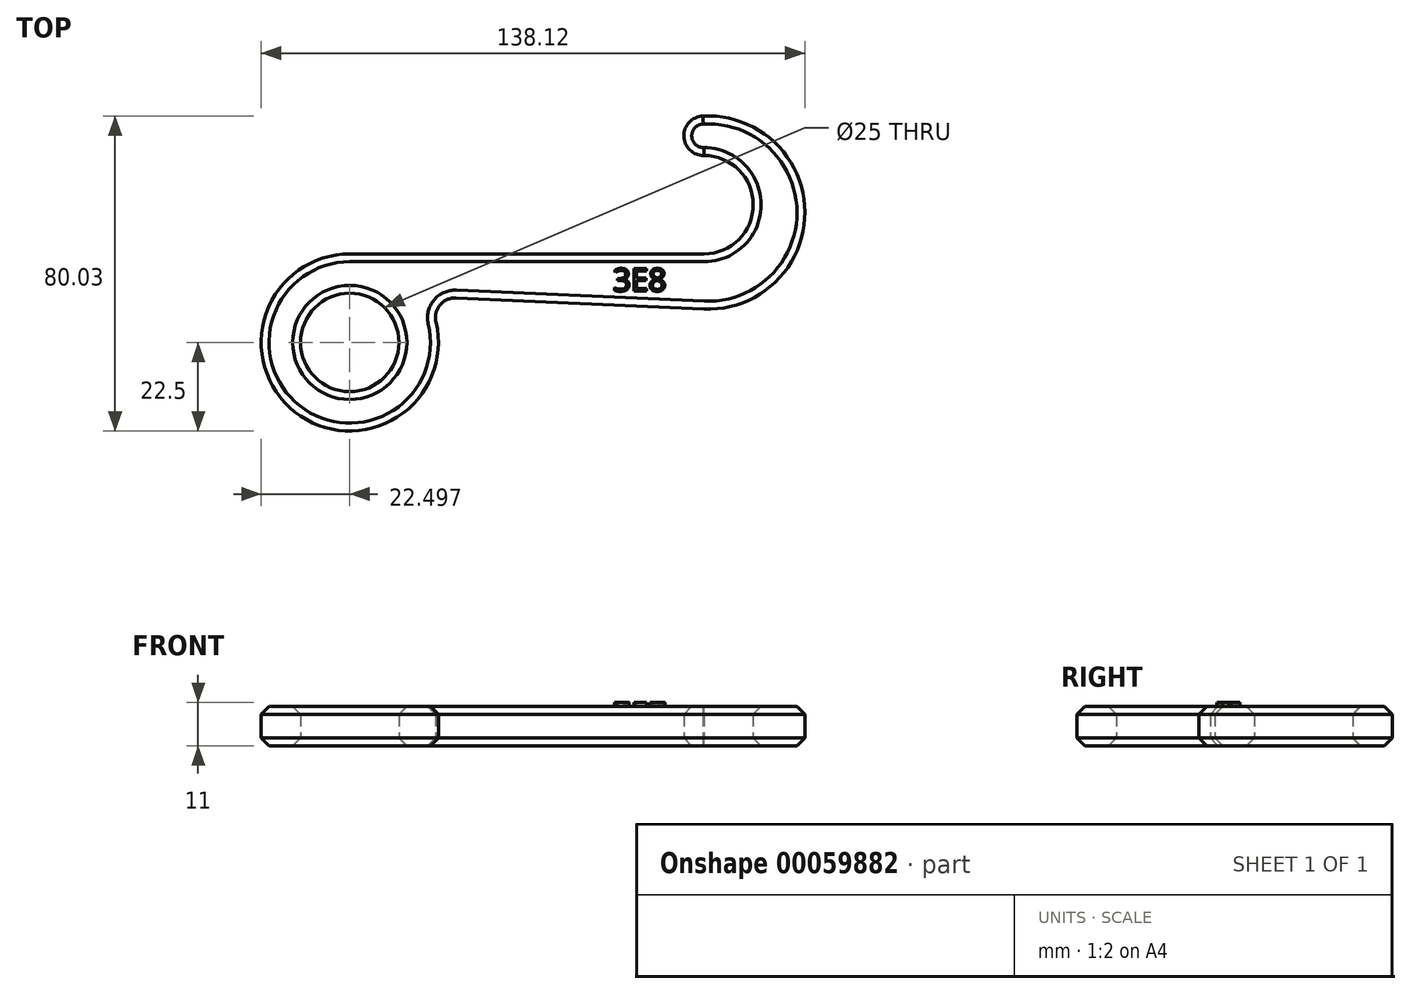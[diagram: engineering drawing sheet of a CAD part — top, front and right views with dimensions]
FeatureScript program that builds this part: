
annotation { "Feature Type Name" : "Feature", "Feature Type Description" : "" }
export const myFeature = defineFeature(function(context is Context, id is Id, definition is map)
    precondition{}
    {
        {
            var Q0;
            Q0=qCreatedBy(makeId("Top.planeOp"),FACE);
            var sketch = newSketch(context, id + "F0", { "sketchPlane" : qUnion([Q0])});
            skCircle(sketch, "E0", {"center": v(0, 0) * mm, "radius": 12.5 * mm});
            skCircle(sketch, "E1", {"center": v(0, 0) * mm, "radius": 22.5 * mm});
            skLineSegment(sketch, "E2", {"start": v(0, 12.5) * mm, "end": v(0, 22.5) * mm, "construction": true});
            skLineSegment(sketch, "E3", {"start": v(0, 22.5) * mm, "end": v(90, 22.5) * mm});
            skArc(sketch, "E4", {"start": v(90, 22.5) * mm, "mid": v(102.5, 35) * mm, "end": v(90, 47.5) * mm});
            skArc(sketch, "E5", {"start": v(89.75, 57.5) * mm, "mid": v(84.88, 52.37) * mm, "end": v(90, 47.5) * mm});
            skLineSegment(sketch, "E6", {"start": v(89.75, 57.5) * mm, "end": v(90, 47.5) * mm, "construction": true});
            skPoint(sketch, "E7", {"position": v(59.76, 12.5) * mm});
            skLineSegment(sketch, "E8", {"start": v(90, 8.5) * mm, "end": v(90, 22.5) * mm, "construction": true});
            skLineSegment(sketch, "E9", {"start": v(90, 8.5) * mm, "end": v(0, 12.5) * mm});
            skArc(sketch, "E10", {"start": v(90, 8.5) * mm, "mid": v(115.62, 33.13) * mm, "end": v(89.75, 57.5) * mm});
            skSolve(sketch);
        }
        {
            var Q0;
            Q0 = qSketchRegion(id + "F0", true);
            extrude(context, id + "F1", {"entities" : qUnion([Q0]), "depth" : 10 * mm});
        }
        {
            var Q0;
            Q0=makeQuery(id+"F1.opExtrude","SWEPT_EDGE",EDGE,{"disambiguationData":[OSD([sQuery(id+"F0.wireOp",EDGE,"E1"),sQuery(id+"F0.wireOp",EDGE,"HazXNHMS-Q4m4-70EI-QaVJ-TpPeL8ySbxYI")])]});
            fillet(context, id + "F2", {"entities" : qUnion([Q0]), "radius" : 5 * mm, "tangentPropagation" : true, "allowEdgeOverflow" : false});
        }
        {
            var Q0;
            Q0=makeQuery(id+"F1.opExtrude","CAP_FACE",FACE,{"disambiguationData":[OSD([sQuery(id+"F0.wireOp",EDGE,"E0"),sQuery(id+"F0.wireOp",EDGE,"E1"),sQuery(id+"F0.wireOp",EDGE,"E3"),sQuery(id+"F0.wireOp",EDGE,"HazXNHMS-Q4m4-70EI-QaVJ-TpPeL8ySbxYI"),sQuery(id+"F0.wireOp",EDGE,"E4"),sQuery(id+"F0.wireOp",EDGE,"a1ac120a-fc83-4f19-9212-36d8e5cb0573"),sQuery(id+"F0.wireOp",EDGE,"E5")])],"isStart":false});
            var sketch = newSketch(context, id + "F3", { "sketchPlane" : qUnion([Q0])});
            skText(sketch, "E11", { "text": "3E8", "fontName": "OpenSans-Regular.ttf"});
            skLineSegment(sketch, "E12", {"start": v(58.5, 9.9) * mm, "end": v(58.5, 12.9) * mm, "construction": true});
            const initialGuessF3  = {"E11": [0.06684, 0.01305, 1, 0, 0.00576]};
            skSetInitialGuess(sketch, initialGuessF3);
            skSolve(sketch);
        }
        {
            var Q0;
            Q0 = qSketchRegion(id + "F3", true);
            extrude(context, id + "F4", {"entities" : qUnion([Q0]), "operationType" : NewBodyOperationType.ADD, "depth" : 1 * mm});
        }
        {
            var Q0;
            Q0=makeQuery(id+"F1.opExtrude","SWEPT_BODY",BODY,{"disambiguationData":[OSD([sQuery(id+"F0.wireOp",EDGE,"E0"),sQuery(id+"F0.wireOp",EDGE,"E1"),sQuery(id+"F0.wireOp",EDGE,"E3"),sQuery(id+"F0.wireOp",EDGE,"HazXNHMS-Q4m4-70EI-QaVJ-TpPeL8ySbxYI"),sQuery(id+"F0.wireOp",EDGE,"E4"),sQuery(id+"F0.wireOp",EDGE,"a1ac120a-fc83-4f19-9212-36d8e5cb0573"),sQuery(id+"F0.wireOp",EDGE,"E5")])]});
            var Q1;
            Q1=sQuery(id+"F0.wireOp",VERTEX,"E7");
            var Q2;
            Q2=sQuery(id+"F0.wireOp",VERTEX,"E1.center");
            transform(context, id + "F5", {"entities" : qUnion([Q0]), "transformType" : TransformType.TRANSLATION_ENTITY, "oppositeDirectionEntity" : false, "transformLine" : qUnion([Q1, Q2]), "makeCopy" : false});
        }
        {
            var Q0;
            Q0=makeQuery(id+"F1.opExtrude","CAP_EDGE",EDGE,{"disambiguationData":[OSD([sQuery(id+"F0.wireOp",EDGE,"E9")])],"isStart":false});
            var Q1;
            Q1=makeQuery(id+"F1.opExtrude","CAP_EDGE",EDGE,{"disambiguationData":[OSD([sQuery(id+"F0.wireOp",EDGE,"E5")])],"isStart":false});
            var Q2;
            Q2=makeQuery(id+"F1.opExtrude","CAP_EDGE",EDGE,{"disambiguationData":[OSD([sQuery(id+"F0.wireOp",EDGE,"E9")])],"isStart":true});
            var Q3;
            Q3=makeQuery(id+"F1.opExtrude","CAP_EDGE",EDGE,{"disambiguationData":[OSD([sQuery(id+"F0.wireOp",EDGE,"E5")])],"isStart":true});
            var Q4;
            Q4=makeQuery(id+"F1.opExtrude","CAP_EDGE",EDGE,{"disambiguationData":[OSD([sQuery(id+"F0.wireOp",EDGE,"E0")])],"isStart":true});
            var Q5;
            Q5=makeQuery(id+"F1.opExtrude","CAP_EDGE",EDGE,{"disambiguationData":[OSD([sQuery(id+"F0.wireOp",EDGE,"E0")])],"isStart":false});
            chamfer(context, id + "F6", {"entities" : qUnion([Q0, Q1, Q2, Q3, Q4, Q5]), "width" : 2 * mm, "tangentPropagation" : true});
        }
    });
